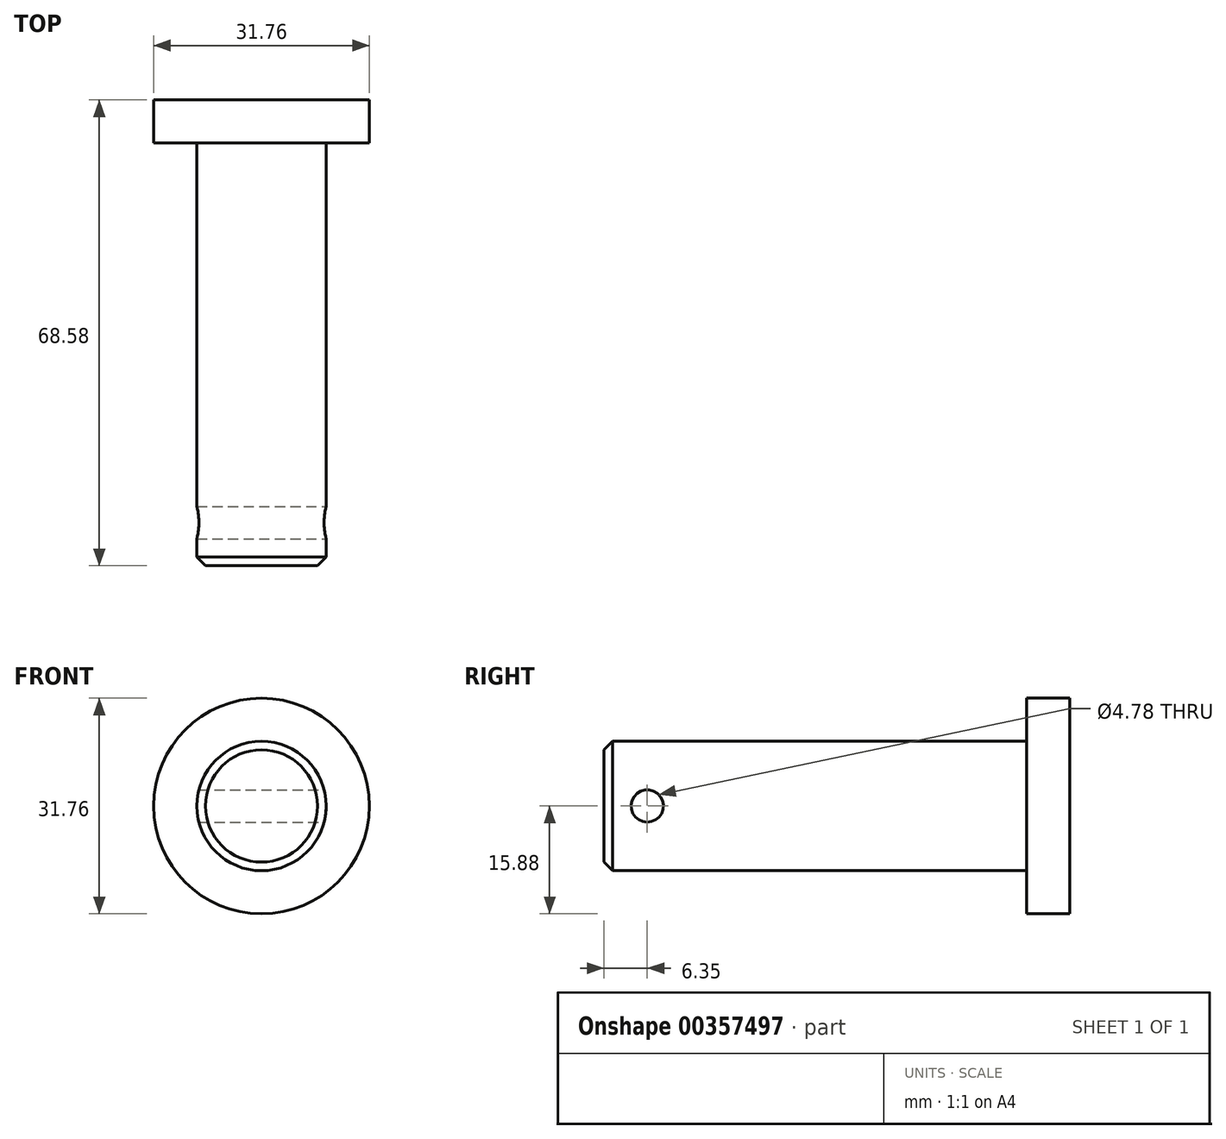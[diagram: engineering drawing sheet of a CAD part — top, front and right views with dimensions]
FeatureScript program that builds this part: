
annotation { "Feature Type Name" : "Feature", "Feature Type Description" : "" }
export const myFeature = defineFeature(function(context is Context, id is Id, definition is map)
    precondition{}
    {
        {
            var Q0;
            Q0=qCreatedBy(makeId("Front.planeOp"),FACE);
            var sketch = newSketch(context, id + "F0", { "sketchPlane" : qUnion([Q0])});
            skCircle(sketch, "E0", {"center": v(0, 0) * mm, "radius": 15.88 * mm});
            skSolve(sketch);
        }
        {
            var Q0;
            Q0=makeQuery(id+"F0.imprint","IMPRINT",FACE,{"disambiguationData":[TD([[makeQuery(id+"F0.imprint","IMPRINT",EDGE,{"derivedFrom":sQuery(id+"F0.wireOp",EDGE,"E0")}),1.0]])]});
            extrude(context, id + "F1", {"entities" : qUnion([Q0]), "depth" : 6.35 * mm});
        }
        {
            var Q0;
            Q0=makeQuery(id+"F1.opExtrude","CAP_FACE",FACE,{"disambiguationData":[OSD([sQuery(id+"F0.wireOp",EDGE,"E0")])],"isStart":false});
            var sketch = newSketch(context, id + "F2", { "sketchPlane" : qUnion([Q0])});
            skCircle(sketch, "E1", {"center": v(0, 0) * mm, "radius": 9.53 * mm});
            skSolve(sketch);
        }
        {
            var Q0;
            Q0=makeQuery(id+"F2.imprint","IMPRINT",FACE,{"disambiguationData":[TD([[makeQuery(id+"F2.imprint","IMPRINT",EDGE,{"derivedFrom":sQuery(id+"F2.wireOp",EDGE,"E1")}),1.0]])]});
            extrude(context, id + "F3", {"entities" : qUnion([Q0]), "operationType" : NewBodyOperationType.ADD, "depth" : 62.23 * mm});
        }
        {
            var Q0;
            Q0=makeQuery(id+"F3.opExtrude","CAP_EDGE",EDGE,{"disambiguationData":[OSD([sQuery(id+"F2.wireOp",EDGE,"E1")])],"isStart":false});
            chamfer(context, id + "F4", {"entities" : qUnion([Q0]), "chamferType" : ChamferType.OFFSET_ANGLE, "width" : 1.27 * mm, "oppositeDirection" : false, "angle" : 45 * degree, "tangentPropagation" : true});
        }
        {
            var Q0;
            Q0=qCreatedBy(makeId("Right.planeOp"),FACE);
            var sketch = newSketch(context, id + "F5", { "sketchPlane" : qUnion([Q0])});
            skCircle(sketch, "E2", {"center": v(-62.23, 0) * mm, "radius": 2.39 * mm});
            skSolve(sketch);
        }
        {
            var Q0;
            Q0 = qSketchRegion(id + "F5", true);
            extrude(context, id + "F6", {"entities" : qUnion([Q0]), "operationType" : NewBodyOperationType.REMOVE, "endBound" : BoundingType.SYMMETRIC, "oppositeDirection" : true, "depth" : 1397 * mm});
        }
    });
